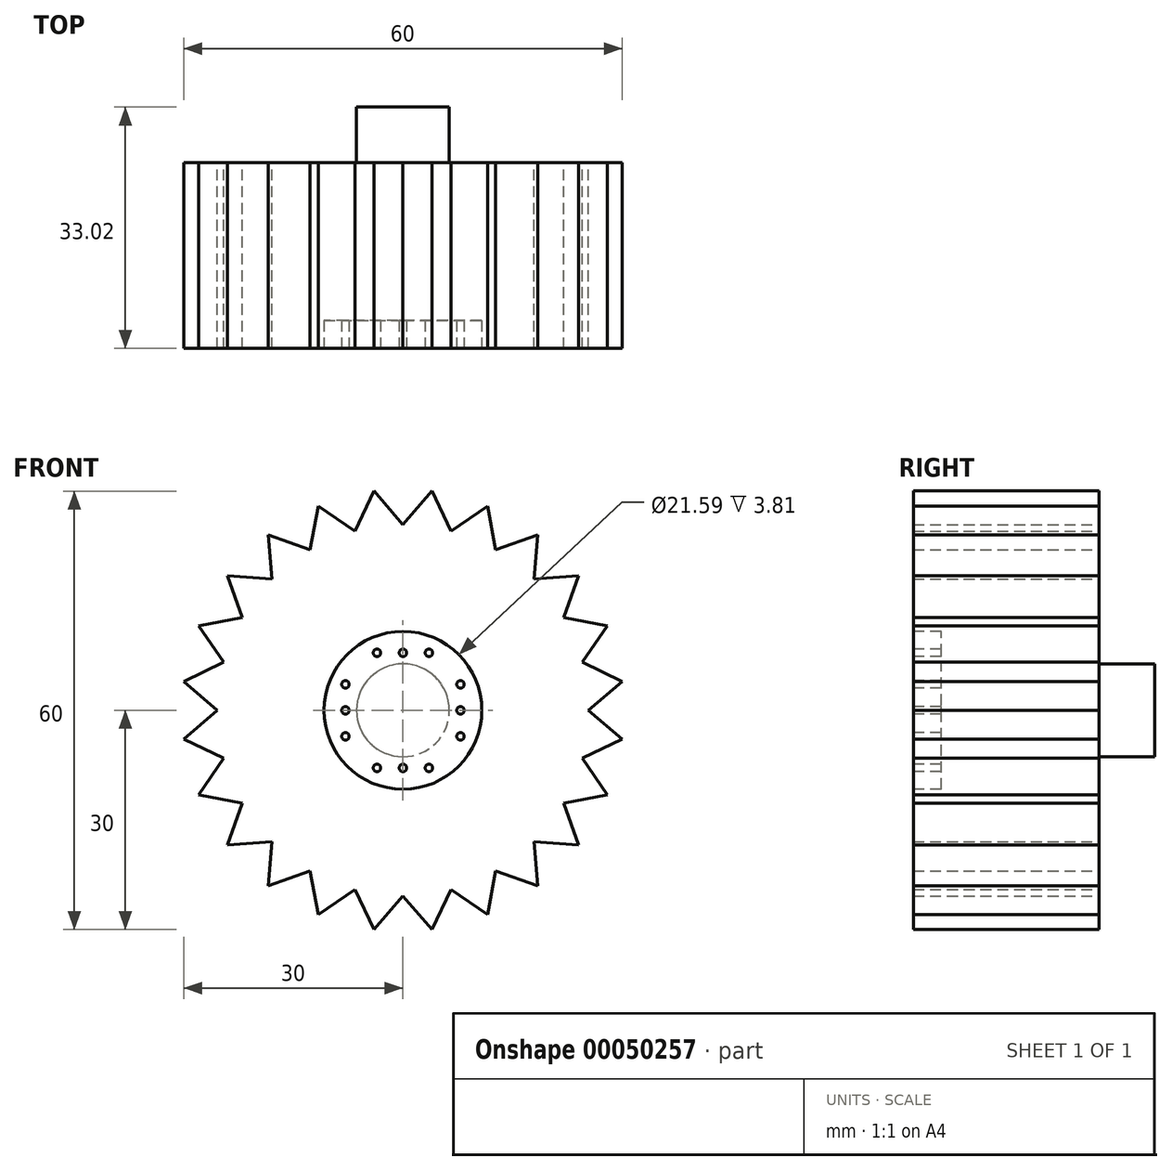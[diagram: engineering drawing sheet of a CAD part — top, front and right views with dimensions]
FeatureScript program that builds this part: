
annotation { "Feature Type Name" : "Feature", "Feature Type Description" : "" }
export const myFeature = defineFeature(function(context is Context, id is Id, definition is map)
    precondition{}
    {
        {
            var Q0;
            Q0=qCreatedBy(makeId("Front.planeOp"),FACE);
            var sketch = newSketch(context, id + "F0", { "sketchPlane" : qUnion([Q0])});
            skCircle(sketch, "E0", {"center": v(0, 0) * mm, "radius": 25.4 * mm});
            skLineSegment(sketch, "E1", {"start": v(0, 0) * mm, "end": v(25.4, 0) * mm});
            skLineSegment(sketch, "E2", {"start": v(0, 0) * mm, "end": v(0, 25.4) * mm});
            skLineSegment(sketch, "E3", {"start": v(0, 0) * mm, "end": v(-25.4, 0) * mm});
            skLineSegment(sketch, "E4", {"start": v(0, 0) * mm, "end": v(0, -25.4) * mm});
            skLineSegment(sketch, "E5", {"start": v(0, 0) * mm, "end": v(24.53, -6.57) * mm});
            skLineSegment(sketch, "E6", {"start": v(25.4, 0) * mm, "end": v(24.53, -6.57) * mm});
            skLineSegment(sketch, "E7", {"start": v(24.97, -3.29) * mm, "end": v(30, -3.95) * mm});
            skLineSegment(sketch, "E8", {"start": v(25.4, 0) * mm, "end": v(30, -3.95) * mm});
            skLineSegment(sketch, "E9", {"start": v(24.53, -6.57) * mm, "end": v(30, -3.95) * mm});
            skLineSegment(sketch, "E10", {"start": v(0, 0) * mm, "end": v(24.53, 6.57) * mm});
            skLineSegment(sketch, "E11", {"start": v(0, 0) * mm, "end": v(22, 12.7) * mm});
            skLineSegment(sketch, "E12", {"start": v(0, 0) * mm, "end": v(17.96, 17.96) * mm});
            skLineSegment(sketch, "E13", {"start": v(0, 0) * mm, "end": v(12.7, 22) * mm});
            skLineSegment(sketch, "E14", {"start": v(0, 0) * mm, "end": v(6.57, 24.53) * mm});
            skLineSegment(sketch, "E15", {"start": v(0, 0) * mm, "end": v(-6.57, -24.53) * mm});
            skLineSegment(sketch, "E16", {"start": v(0, 0) * mm, "end": v(22, -12.7) * mm});
            skLineSegment(sketch, "E17", {"start": v(0, 0) * mm, "end": v(17.96, -17.96) * mm});
            skLineSegment(sketch, "E18", {"start": v(0, 0) * mm, "end": v(12.7, -22) * mm});
            skLineSegment(sketch, "E19", {"start": v(0, 0) * mm, "end": v(6.57, -24.53) * mm});
            skLineSegment(sketch, "E20", {"start": v(0, 0) * mm, "end": v(-12.7, -22) * mm});
            skLineSegment(sketch, "E21", {"start": v(0, 0) * mm, "end": v(-17.96, -17.96) * mm});
            skLineSegment(sketch, "E22", {"start": v(0, 0) * mm, "end": v(-22, -12.7) * mm});
            skLineSegment(sketch, "E23", {"start": v(0, 0) * mm, "end": v(-24.53, -6.57) * mm});
            skLineSegment(sketch, "E24", {"start": v(0, 0) * mm, "end": v(-24.53, 6.57) * mm});
            skLineSegment(sketch, "E25", {"start": v(0, 0) * mm, "end": v(-22, 12.7) * mm});
            skLineSegment(sketch, "E26", {"start": v(0, 0) * mm, "end": v(-17.96, 17.96) * mm});
            skLineSegment(sketch, "E27", {"start": v(0, 0) * mm, "end": v(-12.7, 22) * mm});
            skLineSegment(sketch, "E28", {"start": v(0, 0) * mm, "end": v(-6.57, 24.53) * mm});
            skLineSegment(sketch, "E29", {"start": v(25.4, 0) * mm, "end": v(24.53, 6.57) * mm});
            skLineSegment(sketch, "E30", {"start": v(22, 12.7) * mm, "end": v(17.96, 17.96) * mm});
            skLineSegment(sketch, "E31", {"start": v(12.7, 22) * mm, "end": v(6.57, 24.53) * mm});
            skLineSegment(sketch, "E32", {"start": v(0, 25.4) * mm, "end": v(-6.57, 24.53) * mm});
            skLineSegment(sketch, "E33", {"start": v(-12.7, 22) * mm, "end": v(-17.96, 17.96) * mm});
            skLineSegment(sketch, "E34", {"start": v(-22, 12.7) * mm, "end": v(-24.53, 6.57) * mm});
            skLineSegment(sketch, "E35", {"start": v(-25.4, 0) * mm, "end": v(-24.53, -6.57) * mm});
            skLineSegment(sketch, "E36", {"start": v(-22, -12.7) * mm, "end": v(-17.96, -17.96) * mm});
            skLineSegment(sketch, "E37", {"start": v(-12.7, -22) * mm, "end": v(-6.57, -24.53) * mm});
            skLineSegment(sketch, "E38", {"start": v(0, -25.4) * mm, "end": v(6.57, -24.53) * mm});
            skLineSegment(sketch, "E39", {"start": v(12.7, -22) * mm, "end": v(17.96, -17.96) * mm});
            skLineSegment(sketch, "E40", {"start": v(22, -12.7) * mm, "end": v(24.53, -6.57) * mm});
            skLineSegment(sketch, "E41", {"start": v(24.53, 6.57) * mm, "end": v(22, 12.7) * mm});
            skLineSegment(sketch, "E42", {"start": v(17.96, 17.96) * mm, "end": v(12.7, 22) * mm});
            skLineSegment(sketch, "E43", {"start": v(6.57, 24.53) * mm, "end": v(0, 25.4) * mm});
            skLineSegment(sketch, "E44", {"start": v(-6.57, 24.53) * mm, "end": v(-12.7, 22) * mm});
            skLineSegment(sketch, "E45", {"start": v(-17.96, 17.96) * mm, "end": v(-22, 12.7) * mm});
            skLineSegment(sketch, "E46", {"start": v(-24.53, 6.57) * mm, "end": v(-25.4, 0) * mm});
            skLineSegment(sketch, "E47", {"start": v(-24.53, -6.57) * mm, "end": v(-22, -12.7) * mm});
            skLineSegment(sketch, "E48", {"start": v(-17.96, -17.96) * mm, "end": v(-12.7, -22) * mm});
            skLineSegment(sketch, "E49", {"start": v(-6.57, -24.53) * mm, "end": v(0, -25.4) * mm});
            skLineSegment(sketch, "E50", {"start": v(6.57, -24.53) * mm, "end": v(12.7, -22) * mm});
            skLineSegment(sketch, "E51", {"start": v(17.96, -17.96) * mm, "end": v(22, -12.7) * mm});
            skLineSegment(sketch, "E52", {"start": v(24.97, 3.29) * mm, "end": v(30, 3.95) * mm});
            skLineSegment(sketch, "E53", {"start": v(30, 3.95) * mm, "end": v(24.53, 6.57) * mm});
            skLineSegment(sketch, "E54", {"start": v(30, 3.95) * mm, "end": v(25.4, 0) * mm});
            skPoint(sketch, "E55.startSnap0", {"position": v(23.27, 9.64) * mm});
            skLineSegment(sketch, "E56", {"start": v(23.27, 9.64) * mm, "end": v(27.96, 11.58) * mm});
            skLineSegment(sketch, "E57", {"start": v(27.96, 11.58) * mm, "end": v(22, 12.7) * mm});
            skLineSegment(sketch, "E58", {"start": v(24.53, 6.57) * mm, "end": v(27.96, 11.58) * mm});
            skLineSegment(sketch, "E59", {"start": v(19.98, 15.33) * mm, "end": v(24, 18.42) * mm});
            skLineSegment(sketch, "E60", {"start": v(24, 18.42) * mm, "end": v(22, 12.7) * mm});
            skLineSegment(sketch, "E61", {"start": v(24, 18.42) * mm, "end": v(17.96, 17.96) * mm});
            skLineSegment(sketch, "E62", {"start": v(15.33, 19.98) * mm, "end": v(18.42, 24) * mm});
            skLineSegment(sketch, "E63", {"start": v(18.42, 24) * mm, "end": v(17.96, 17.96) * mm});
            skLineSegment(sketch, "E64", {"start": v(18.42, 24) * mm, "end": v(12.7, 22) * mm});
            skLineSegment(sketch, "E65", {"start": v(9.64, 23.27) * mm, "end": v(11.58, 27.96) * mm});
            skLineSegment(sketch, "E66", {"start": v(11.58, 27.96) * mm, "end": v(12.7, 22) * mm});
            skLineSegment(sketch, "E67", {"start": v(11.58, 27.96) * mm, "end": v(6.57, 24.53) * mm});
            skLineSegment(sketch, "E68", {"start": v(3.29, 24.97) * mm, "end": v(3.95, 30) * mm});
            skLineSegment(sketch, "E69", {"start": v(3.95, 30) * mm, "end": v(6.57, 24.53) * mm});
            skLineSegment(sketch, "E70", {"start": v(3.95, 30) * mm, "end": v(0, 25.4) * mm});
            skLineSegment(sketch, "E71", {"start": v(-3.29, 24.97) * mm, "end": v(-3.95, 30) * mm});
            skLineSegment(sketch, "E72", {"start": v(-3.95, 30) * mm, "end": v(0, 25.4) * mm});
            skLineSegment(sketch, "E73", {"start": v(-3.95, 30) * mm, "end": v(-6.57, 24.53) * mm});
            skLineSegment(sketch, "E74", {"start": v(-9.64, 23.27) * mm, "end": v(-11.58, 27.96) * mm});
            skLineSegment(sketch, "E75", {"start": v(-11.58, 27.96) * mm, "end": v(-6.57, 24.53) * mm});
            skLineSegment(sketch, "E76", {"start": v(-11.58, 27.96) * mm, "end": v(-12.7, 22) * mm});
            skLineSegment(sketch, "E77", {"start": v(-15.33, 19.98) * mm, "end": v(-18.42, 24) * mm});
            skLineSegment(sketch, "E78", {"start": v(-18.42, 24) * mm, "end": v(-17.96, 17.96) * mm});
            skLineSegment(sketch, "E79", {"start": v(-12.7, 22) * mm, "end": v(-18.42, 24) * mm});
            skLineSegment(sketch, "E80", {"start": v(-19.98, 15.33) * mm, "end": v(-24, 18.42) * mm});
            skLineSegment(sketch, "E81", {"start": v(-24, 18.42) * mm, "end": v(-22, 12.7) * mm});
            skLineSegment(sketch, "E82", {"start": v(-17.96, 17.96) * mm, "end": v(-24, 18.42) * mm});
            skLineSegment(sketch, "E83", {"start": v(-23.27, 9.64) * mm, "end": v(-27.96, 11.58) * mm});
            skLineSegment(sketch, "E84", {"start": v(-27.96, 11.58) * mm, "end": v(-22, 12.7) * mm});
            skLineSegment(sketch, "E85", {"start": v(-27.96, 11.58) * mm, "end": v(-24.53, 6.57) * mm});
            skLineSegment(sketch, "E86", {"start": v(-24.97, 3.29) * mm, "end": v(-30, 3.95) * mm});
            skLineSegment(sketch, "E87", {"start": v(-30, 3.95) * mm, "end": v(-25.4, 0) * mm});
            skLineSegment(sketch, "E88", {"start": v(-30, 3.95) * mm, "end": v(-24.53, 6.57) * mm});
            skLineSegment(sketch, "E89", {"start": v(-24.97, -3.29) * mm, "end": v(-30, -3.95) * mm});
            skLineSegment(sketch, "E90", {"start": v(-30, -3.95) * mm, "end": v(-24.53, -6.57) * mm});
            skLineSegment(sketch, "E91", {"start": v(-30, -3.95) * mm, "end": v(-25.4, 0) * mm});
            skLineSegment(sketch, "E92", {"start": v(-23.27, -9.64) * mm, "end": v(-27.96, -11.58) * mm});
            skLineSegment(sketch, "E93", {"start": v(-27.96, -11.58) * mm, "end": v(-24.53, -6.57) * mm});
            skLineSegment(sketch, "E94", {"start": v(-22, -12.7) * mm, "end": v(-27.96, -11.58) * mm});
            skLineSegment(sketch, "E95", {"start": v(-19.98, -15.33) * mm, "end": v(-24, -18.42) * mm});
            skLineSegment(sketch, "E96", {"start": v(-24, -18.42) * mm, "end": v(-22, -12.7) * mm});
            skLineSegment(sketch, "E97", {"start": v(-17.96, -17.96) * mm, "end": v(-24, -18.42) * mm});
            skLineSegment(sketch, "E98", {"start": v(-15.33, -19.98) * mm, "end": v(-18.42, -24) * mm});
            skLineSegment(sketch, "E99", {"start": v(-18.42, -24) * mm, "end": v(-17.96, -17.96) * mm});
            skLineSegment(sketch, "E100", {"start": v(-12.7, -22) * mm, "end": v(-18.42, -24) * mm});
            skLineSegment(sketch, "E101", {"start": v(-9.64, -23.27) * mm, "end": v(-11.58, -27.96) * mm});
            skLineSegment(sketch, "E102", {"start": v(-11.58, -27.96) * mm, "end": v(-12.7, -22) * mm});
            skLineSegment(sketch, "E103", {"start": v(-6.57, -24.53) * mm, "end": v(-11.58, -27.96) * mm});
            skLineSegment(sketch, "E104", {"start": v(-3.29, -24.97) * mm, "end": v(-3.95, -30) * mm});
            skLineSegment(sketch, "E105", {"start": v(-3.95, -30) * mm, "end": v(-6.57, -24.53) * mm});
            skLineSegment(sketch, "E106", {"start": v(0, -25.4) * mm, "end": v(-3.95, -30) * mm});
            skLineSegment(sketch, "E107", {"start": v(3.29, -24.97) * mm, "end": v(3.95, -30) * mm});
            skLineSegment(sketch, "E108", {"start": v(3.95, -30) * mm, "end": v(0, -25.4) * mm});
            skLineSegment(sketch, "E109", {"start": v(6.57, -24.53) * mm, "end": v(3.95, -30) * mm});
            skLineSegment(sketch, "E110", {"start": v(9.64, -23.27) * mm, "end": v(11.58, -27.96) * mm});
            skLineSegment(sketch, "E111", {"start": v(12.7, -22) * mm, "end": v(11.58, -27.96) * mm});
            skLineSegment(sketch, "E112", {"start": v(11.58, -27.96) * mm, "end": v(6.57, -24.53) * mm});
            skLineSegment(sketch, "E113", {"start": v(15.33, -19.98) * mm, "end": v(18.42, -24) * mm});
            skLineSegment(sketch, "E114", {"start": v(18.42, -24) * mm, "end": v(12.7, -22) * mm});
            skLineSegment(sketch, "E115", {"start": v(17.96, -17.96) * mm, "end": v(18.42, -24) * mm});
            skLineSegment(sketch, "E116", {"start": v(19.98, -15.33) * mm, "end": v(24, -18.42) * mm});
            skLineSegment(sketch, "E117", {"start": v(24, -18.42) * mm, "end": v(17.96, -17.96) * mm});
            skLineSegment(sketch, "E118", {"start": v(22, -12.7) * mm, "end": v(24, -18.42) * mm});
            skLineSegment(sketch, "E119", {"start": v(23.27, -9.64) * mm, "end": v(27.96, -11.58) * mm});
            skLineSegment(sketch, "E120", {"start": v(27.96, -11.58) * mm, "end": v(22, -12.7) * mm});
            skLineSegment(sketch, "E121", {"start": v(24.53, -6.57) * mm, "end": v(27.96, -11.58) * mm});
            skSolve(sketch);
        }
        {
            var Q0;
            Q0 = qSketchRegion(id + "F0", true);
            extrude(context, id + "F1", {"entities" : qUnion([Q0]), "depth" : 25.4 * mm});
        }
        {
            var Q0;
            Q0=makeQuery(id+"F1.opExtrude","CAP_FACE",FACE,{"disambiguationData":[OSD([sQuery(id+"F0.wireOp",EDGE,"E8"),sQuery(id+"F0.wireOp",EDGE,"E9"),sQuery(id+"F0.wireOp",EDGE,"E53"),sQuery(id+"F0.wireOp",EDGE,"E54"),sQuery(id+"F0.wireOp",EDGE,"E57"),sQuery(id+"F0.wireOp",EDGE,"E58"),sQuery(id+"F0.wireOp",EDGE,"E60"),sQuery(id+"F0.wireOp",EDGE,"E61"),sQuery(id+"F0.wireOp",EDGE,"E63"),sQuery(id+"F0.wireOp",EDGE,"E64"),sQuery(id+"F0.wireOp",EDGE,"E66"),sQuery(id+"F0.wireOp",EDGE,"E67"),sQuery(id+"F0.wireOp",EDGE,"E69"),sQuery(id+"F0.wireOp",EDGE,"E70"),sQuery(id+"F0.wireOp",EDGE,"E72"),sQuery(id+"F0.wireOp",EDGE,"E73"),sQuery(id+"F0.wireOp",EDGE,"E75"),sQuery(id+"F0.wireOp",EDGE,"E76"),sQuery(id+"F0.wireOp",EDGE,"E78"),sQuery(id+"F0.wireOp",EDGE,"E79"),sQuery(id+"F0.wireOp",EDGE,"E81"),sQuery(id+"F0.wireOp",EDGE,"E82"),sQuery(id+"F0.wireOp",EDGE,"E84"),sQuery(id+"F0.wireOp",EDGE,"E85"),sQuery(id+"F0.wireOp",EDGE,"E87"),sQuery(id+"F0.wireOp",EDGE,"E88"),sQuery(id+"F0.wireOp",EDGE,"E90"),sQuery(id+"F0.wireOp",EDGE,"E91"),sQuery(id+"F0.wireOp",EDGE,"E93"),sQuery(id+"F0.wireOp",EDGE,"E94"),sQuery(id+"F0.wireOp",EDGE,"E96"),sQuery(id+"F0.wireOp",EDGE,"E97"),sQuery(id+"F0.wireOp",EDGE,"E99"),sQuery(id+"F0.wireOp",EDGE,"E100"),sQuery(id+"F0.wireOp",EDGE,"E102"),sQuery(id+"F0.wireOp",EDGE,"E103"),sQuery(id+"F0.wireOp",EDGE,"E105"),sQuery(id+"F0.wireOp",EDGE,"E106"),sQuery(id+"F0.wireOp",EDGE,"E108"),sQuery(id+"F0.wireOp",EDGE,"E109"),sQuery(id+"F0.wireOp",EDGE,"E111"),sQuery(id+"F0.wireOp",EDGE,"E112"),sQuery(id+"F0.wireOp",EDGE,"E114"),sQuery(id+"F0.wireOp",EDGE,"E115"),sQuery(id+"F0.wireOp",EDGE,"E117"),sQuery(id+"F0.wireOp",EDGE,"E118"),sQuery(id+"F0.wireOp",EDGE,"E120"),sQuery(id+"F0.wireOp",EDGE,"E121")])],"isStart":false});
            var sketch = newSketch(context, id + "F2", { "sketchPlane" : qUnion([Q0])});
            skCircle(sketch, "E122", {"center": v(0, 0) * mm, "radius": 10.8 * mm});
            skLineSegment(sketch, "E123", {"start": v(0, 10.8) * mm, "end": v(0, 8.38) * mm});
            skCircle(sketch, "E124", {"center": v(0, 7.87) * mm, "radius": 0.5 * mm});
            skLineSegment(sketch, "E125", {"start": v(0.5, 7.87) * mm, "end": v(3.05, 7.87) * mm});
            skLineSegment(sketch, "E126", {"start": v(-0.5, 7.87) * mm, "end": v(-3.05, 7.87) * mm});
            skCircle(sketch, "E127", {"center": v(-3.56, 7.87) * mm, "radius": 0.5 * mm});
            skCircle(sketch, "E128", {"center": v(3.56, 7.87) * mm, "radius": 0.5 * mm});
            skLineSegment(sketch, "E129", {"start": v(-10.8, 0) * mm, "end": v(-8.38, 0) * mm});
            skLineSegment(sketch, "E130", {"start": v(10.8, 0) * mm, "end": v(8.38, 0) * mm});
            skLineSegment(sketch, "E131", {"start": v(0, -10.8) * mm, "end": v(0, -8.38) * mm});
            skCircle(sketch, "E132", {"center": v(0, -7.87) * mm, "radius": 0.5 * mm});
            skCircle(sketch, "E133", {"center": v(-7.87, 0) * mm, "radius": 0.5 * mm});
            skCircle(sketch, "E134", {"center": v(7.87, 0) * mm, "radius": 0.5 * mm});
            skLineSegment(sketch, "E135", {"start": v(-7.87, 0.5) * mm, "end": v(-7.87, 3.05) * mm});
            skLineSegment(sketch, "E136", {"start": v(-7.87, -0.5) * mm, "end": v(-7.87, -3.05) * mm});
            skLineSegment(sketch, "E137", {"start": v(7.87, 0.5) * mm, "end": v(7.87, 3.05) * mm});
            skLineSegment(sketch, "E138", {"start": v(7.87, -0.5) * mm, "end": v(7.87, -3.05) * mm});
            skLineSegment(sketch, "E139", {"start": v(0.5, -7.87) * mm, "end": v(3.05, -7.87) * mm});
            skLineSegment(sketch, "E140", {"start": v(-0.5, -7.87) * mm, "end": v(-3.05, -7.87) * mm});
            skCircle(sketch, "E141", {"center": v(-7.87, 3.56) * mm, "radius": 0.5 * mm});
            skCircle(sketch, "E142", {"center": v(-7.87, -3.56) * mm, "radius": 0.5 * mm});
            skCircle(sketch, "E143", {"center": v(7.87, -3.56) * mm, "radius": 0.5 * mm});
            skCircle(sketch, "E144", {"center": v(7.87, 3.56) * mm, "radius": 0.5 * mm});
            skCircle(sketch, "E145", {"center": v(-3.56, -7.87) * mm, "radius": 0.5 * mm});
            skCircle(sketch, "E146", {"center": v(3.56, -7.87) * mm, "radius": 0.5 * mm});
            skSolve(sketch);
        }
        {
            var Q0;
            Q0 = qSketchRegion(id + "F2", true);
            extrude(context, id + "F3", {"entities" : qUnion([Q0]), "operationType" : NewBodyOperationType.REMOVE, "oppositeDirection" : true, "depth" : 3.8 * mm});
        }
        {
            var Q0;
            Q0=makeQuery(id+"F1.opExtrude","CAP_FACE",FACE,{"disambiguationData":[OSD([sQuery(id+"F0.wireOp",EDGE,"E8"),sQuery(id+"F0.wireOp",EDGE,"E9"),sQuery(id+"F0.wireOp",EDGE,"E53"),sQuery(id+"F0.wireOp",EDGE,"E54"),sQuery(id+"F0.wireOp",EDGE,"E57"),sQuery(id+"F0.wireOp",EDGE,"E58"),sQuery(id+"F0.wireOp",EDGE,"E60"),sQuery(id+"F0.wireOp",EDGE,"E61"),sQuery(id+"F0.wireOp",EDGE,"E63"),sQuery(id+"F0.wireOp",EDGE,"E64"),sQuery(id+"F0.wireOp",EDGE,"E66"),sQuery(id+"F0.wireOp",EDGE,"E67"),sQuery(id+"F0.wireOp",EDGE,"E69"),sQuery(id+"F0.wireOp",EDGE,"E70"),sQuery(id+"F0.wireOp",EDGE,"E72"),sQuery(id+"F0.wireOp",EDGE,"E73"),sQuery(id+"F0.wireOp",EDGE,"E75"),sQuery(id+"F0.wireOp",EDGE,"E76"),sQuery(id+"F0.wireOp",EDGE,"E78"),sQuery(id+"F0.wireOp",EDGE,"E79"),sQuery(id+"F0.wireOp",EDGE,"E81"),sQuery(id+"F0.wireOp",EDGE,"E82"),sQuery(id+"F0.wireOp",EDGE,"E84"),sQuery(id+"F0.wireOp",EDGE,"E85"),sQuery(id+"F0.wireOp",EDGE,"E87"),sQuery(id+"F0.wireOp",EDGE,"E88"),sQuery(id+"F0.wireOp",EDGE,"E90"),sQuery(id+"F0.wireOp",EDGE,"E91"),sQuery(id+"F0.wireOp",EDGE,"E93"),sQuery(id+"F0.wireOp",EDGE,"E94"),sQuery(id+"F0.wireOp",EDGE,"E96"),sQuery(id+"F0.wireOp",EDGE,"E97"),sQuery(id+"F0.wireOp",EDGE,"E99"),sQuery(id+"F0.wireOp",EDGE,"E100"),sQuery(id+"F0.wireOp",EDGE,"E102"),sQuery(id+"F0.wireOp",EDGE,"E103"),sQuery(id+"F0.wireOp",EDGE,"E105"),sQuery(id+"F0.wireOp",EDGE,"E106"),sQuery(id+"F0.wireOp",EDGE,"E108"),sQuery(id+"F0.wireOp",EDGE,"E109"),sQuery(id+"F0.wireOp",EDGE,"E111"),sQuery(id+"F0.wireOp",EDGE,"E112"),sQuery(id+"F0.wireOp",EDGE,"E114"),sQuery(id+"F0.wireOp",EDGE,"E115"),sQuery(id+"F0.wireOp",EDGE,"E117"),sQuery(id+"F0.wireOp",EDGE,"E118"),sQuery(id+"F0.wireOp",EDGE,"E120"),sQuery(id+"F0.wireOp",EDGE,"E121")])],"isStart":true});
            var sketch = newSketch(context, id + "F4", { "sketchPlane" : qUnion([Q0])});
            skCircle(sketch, "E147", {"center": v(0, 0) * mm, "radius": 6.35 * mm});
            skSolve(sketch);
        }
        {
            var Q0;
            Q0 = qSketchRegion(id + "F4", true);
            extrude(context, id + "F5", {"entities" : qUnion([Q0]), "operationType" : NewBodyOperationType.ADD, "depth" : 7.62 * mm});
        }
    });
